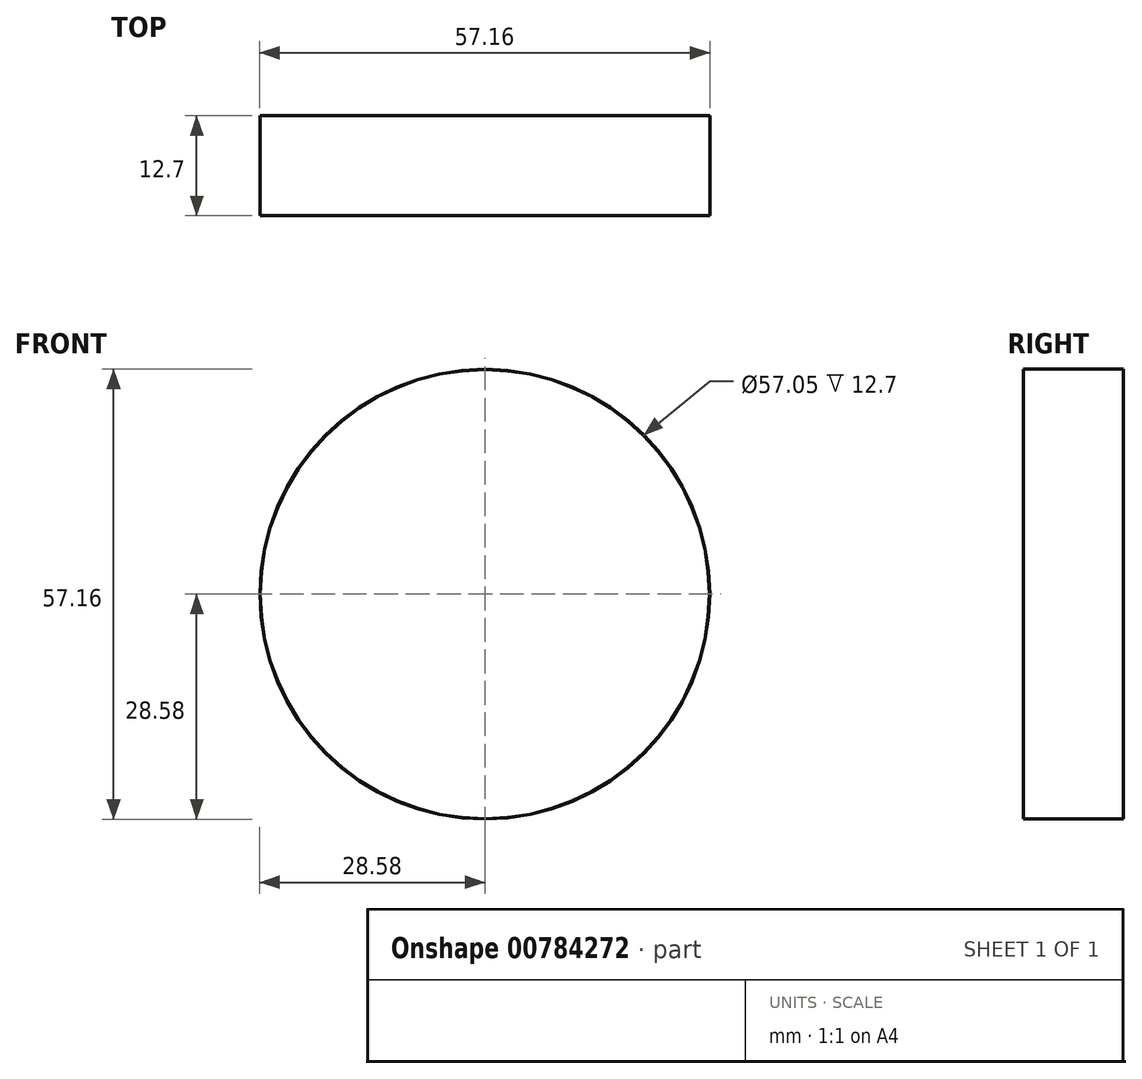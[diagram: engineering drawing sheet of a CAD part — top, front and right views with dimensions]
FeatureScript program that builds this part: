
annotation { "Feature Type Name" : "Feature", "Feature Type Description" : "" }
export const myFeature = defineFeature(function(context is Context, id is Id, definition is map)
    precondition{}
    {
        {
            var Q0;
            Q0=qCreatedBy(makeId("Front.planeOp"),FACE);
            var sketch = newSketch(context, id + "F0", { "sketchPlane" : qUnion([Q0])});
            skCircle(sketch, "E0", {"center": v(0, 0) * mm, "radius": 28.53 * mm});
            skCircle(sketch, "E1", {"center": v(0, 0) * mm, "radius": 28.58 * mm});
            skSolve(sketch);
        }
        {
            var Q0;
            Q0 = qSketchRegion(id + "F0", true);
            extrude(context, id + "F1", {"entities" : qUnion([Q0]), "depth" : 12.7 * mm, "offsetDistance" : 25.4 * mm, "symmetric" : true});
        }
    });
